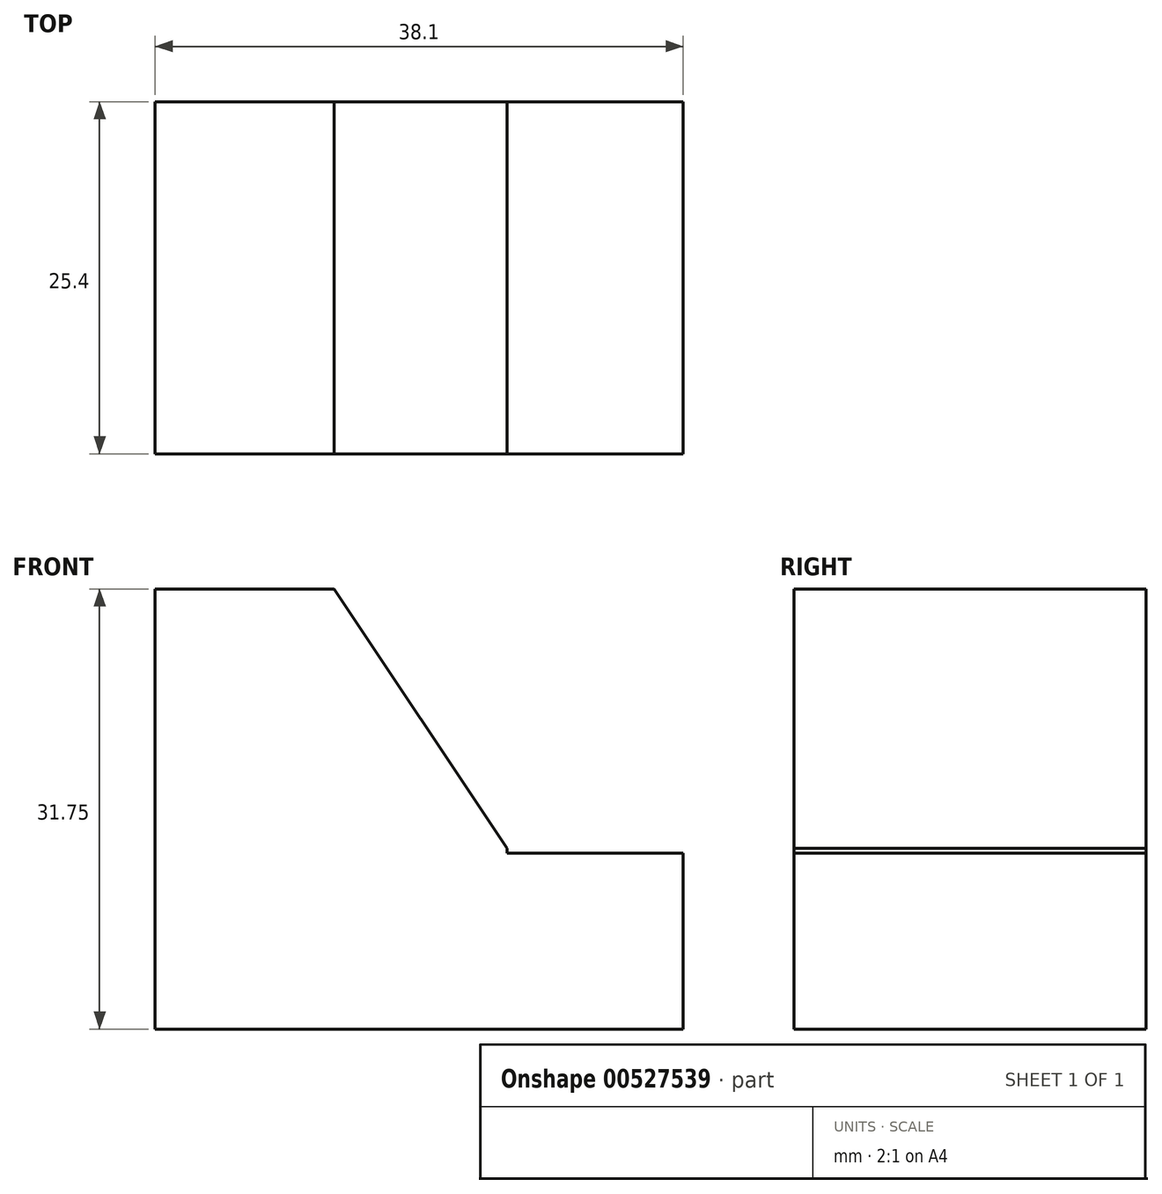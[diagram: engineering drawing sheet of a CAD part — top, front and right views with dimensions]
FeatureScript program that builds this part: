
annotation { "Feature Type Name" : "Feature", "Feature Type Description" : "" }
export const myFeature = defineFeature(function(context is Context, id is Id, definition is map)
    precondition{}
    {
        {
            var Q0;
            Q0=qCreatedBy(makeId("Front.planeOp"),FACE);
            var sketch = newSketch(context, id + "F0", { "sketchPlane" : qUnion([Q0])});
            skLineSegment(sketch, "E0", {"start": v(0, 0) * mm, "end": v(38.1, 0) * mm});
            skLineSegment(sketch, "E1", {"start": v(38.1, 0) * mm, "end": v(38.1, 31.75) * mm});
            skLineSegment(sketch, "E2", {"start": v(38.1, 31.75) * mm, "end": v(0, 31.75) * mm});
            skLineSegment(sketch, "E3", {"start": v(0, 31.75) * mm, "end": v(0, 0) * mm});
            skSolve(sketch);
        }
        {
            var Q0;
            Q0=makeQuery(id+"F0.imprint","IMPRINT",FACE,{"disambiguationData":[TD([[makeQuery(id+"F0.imprint","IMPRINT",EDGE,{"derivedFrom":sQuery(id+"F0.wireOp",EDGE,"E0")}),1.0]])]});
            extrude(context, id + "F1", {"entities" : qUnion([Q0]), "depth" : 25.4 * mm, "offsetDistance" : 25.4 * mm});
        }
        {
            var Q0;
            Q0=makeQuery(id+"F1.opExtrude","SWEPT_FACE",FACE,{"disambiguationData":[OSD([sQuery(id+"F0.wireOp",EDGE,"E1")])]});
            var sketch = newSketch(context, id + "F2", { "sketchPlane" : qUnion([Q0])});
            skLineSegment(sketch, "E4", {"start": v(0, -1.4) * mm, "end": v(0, 12.7) * mm});
            skLineSegment(sketch, "E5", {"start": v(0, 12.7) * mm, "end": v(-25.4, 12.7) * mm});
            skLineSegment(sketch, "E6", {"start": v(-25.4, 12.7) * mm, "end": v(-25.4, 0) * mm});
            skLineSegment(sketch, "E7", {"start": v(-25.4, 0) * mm, "end": v(0, 0) * mm});
            skSolve(sketch);
        }
        {
            var Q0;
            Q0=makeQuery(id+"F1.opExtrude","CAP_FACE",FACE,{"disambiguationData":[OSD([sQuery(id+"F0.wireOp",EDGE,"E0"),sQuery(id+"F0.wireOp",EDGE,"E1"),sQuery(id+"F0.wireOp",EDGE,"E2"),sQuery(id+"F0.wireOp",EDGE,"E3")])],"isStart":false});
            var sketch = newSketch(context, id + "F3", { "sketchPlane" : qUnion([Q0])});
            skLineSegment(sketch, "E8", {"start": v(38.1, 12.7) * mm, "end": v(25.4, 12.7) * mm});
            skLineSegment(sketch, "E9", {"start": v(25.4, 12.7) * mm, "end": v(25.4, 0) * mm});
            skLineSegment(sketch, "E10", {"start": v(25.4, 0) * mm, "end": v(38.1, 0) * mm});
            skLineSegment(sketch, "E11", {"start": v(38.1, 0) * mm, "end": v(38.1, 12.7) * mm});
            skSolve(sketch);
        }
        {
            var Q0;
            {var subQ0=sQuery(id+"F2.wireOp",EDGE,"E5");Q0=makeQuery(id+"F2.imprint","IMPRINT",FACE,{"disambiguationData":[TD([[makeQuery(id+"F2.imprint","IMPRINT",EDGE,{"derivedFrom":subQ0}),-1.0]])]});}
            extrude(context, id + "F4", {"entities" : qUnion([Q0]), "operationType" : NewBodyOperationType.REMOVE, "oppositeDirection" : true, "depth" : 12.7 * mm, "offsetDistance" : 25.4 * mm});
        }
        {
            var Q0;
            {var subQ5=sQuery(id+"F3.wireOp",EDGE,"E8");Q0=makeQuery(id+"F3.imprint","IMPRINT",FACE,{"disambiguationData":[TD([[makeQuery(id+"F3.imprint","IMPRINT",EDGE,{"derivedFrom":subQ5}),-1.0]])]});}
            var sketch = newSketch(context, id + "F5", { "sketchPlane" : qUnion([Q0])});
            skLineSegment(sketch, "E12", {"start": v(25.6, 12.72) * mm, "end": v(25.6, 31.77) * mm});
            skLineSegment(sketch, "E13", {"start": v(25.6, 31.77) * mm, "end": v(12.9, 31.77) * mm});
            skLineSegment(sketch, "E14", {"start": v(12.9, 31.77) * mm, "end": v(25.6, 12.72) * mm});
            skSolve(sketch);
        }
        {
            var Q0;
            {var subQ0=sQuery(id+"F5.wireOp",EDGE,"E14");var subQ1=sQuery(id+"F5.wireOp",EDGE,"E12");var subQ2=makeQuery(id+"F5.imprint","INTERSECT",VERTEX,{"derivedFrom":[subQ1,subQ0]});Q0=makeQuery(id+"F5.imprint","IMPRINT",FACE,{"disambiguationData":[TD([[makeQuery(id+"F5.imprint","IMPRINT",EDGE,{"disambiguationData":[TD([[subQ2,-1.0]])],"derivedFrom":subQ1}),1.0]])]});}
            extrude(context, id + "F6", {"entities" : qUnion([Q0]), "operationType" : NewBodyOperationType.REMOVE, "endBound" : BoundingType.THROUGH_ALL, "oppositeDirection" : true, "depth" : 25.4 * mm, "offsetDistance" : 25.4 * mm});
        }
    });
